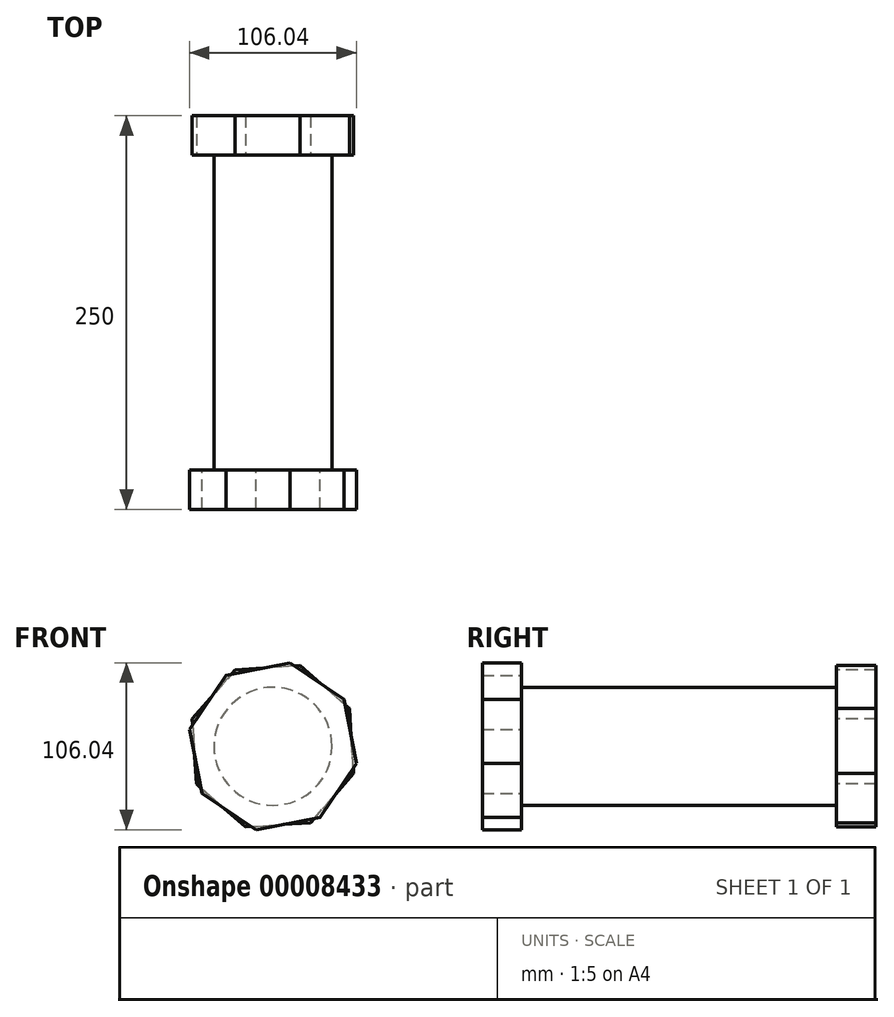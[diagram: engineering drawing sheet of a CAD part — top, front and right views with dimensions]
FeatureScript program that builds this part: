
annotation { "Feature Type Name" : "Feature", "Feature Type Description" : "" }
export const myFeature = defineFeature(function(context is Context, id is Id, definition is map)
    precondition{}
    {
        {
            var Q0;
            Q0=qCreatedBy(makeId("Front.planeOp"),FACE);
            var sketch = newSketch(context, id + "F0", { "sketchPlane" : qUnion([Q0])});
            skCircle(sketch, "E0", {"center": v(0, 0) * mm, "radius": 37.5 * mm});
            skSolve(sketch);
        }
        {
            var Q0;
            Q0 = qSketchRegion(id + "F0", true);
            extrude(context, id + "F1", {"entities" : qUnion([Q0]), "depth" : 200 * mm});
        }
        {
            var Q0;
            Q0=makeQuery(id+"F1.opExtrude","CAP_FACE",FACE,{"disambiguationData":[OSD([sQuery(id+"F0.wireOp",EDGE,"E0")])],"isStart":false});
            var sketch = newSketch(context, id + "F2", { "sketchPlane" : qUnion([Q0])});
            skCircle(sketch, "E1.cCircle", {"center": v(0, 0) * mm, "radius": 50 * mm, "construction": true});
            skLineSegment(sketch, "E1.0", {"start": v(10.83, 53.02) * mm, "end": v(45.15, 29.83) * mm});
            skLineSegment(sketch, "E1.1", {"start": v(45.15, 29.83) * mm, "end": v(53.02, -10.83) * mm});
            skLineSegment(sketch, "E1.2", {"start": v(53.02, -10.83) * mm, "end": v(29.83, -45.15) * mm});
            skLineSegment(sketch, "E1.3", {"start": v(29.83, -45.15) * mm, "end": v(-10.83, -53.02) * mm});
            skLineSegment(sketch, "E1.4", {"start": v(-10.83, -53.02) * mm, "end": v(-45.15, -29.83) * mm});
            skLineSegment(sketch, "E1.5", {"start": v(-45.15, -29.83) * mm, "end": v(-53.02, 10.83) * mm});
            skLineSegment(sketch, "E1.6", {"start": v(-53.02, 10.83) * mm, "end": v(-29.83, 45.15) * mm});
            skLineSegment(sketch, "E1.7", {"start": v(-29.83, 45.15) * mm, "end": v(10.83, 53.02) * mm});
            skPoint(sketch, "E1.0.midPoint", {"position": v(28, 41.43) * mm});
            skSolve(sketch);
        }
        {
            var Q0;
            Q0 = qSketchRegion(id + "F2", true);
            extrude(context, id + "F3", {"entities" : qUnion([Q0]), "operationType" : NewBodyOperationType.ADD, "depth" : 25 * mm});
        }
        {
            var Q0;
            Q0=makeQuery(id+"F1.opExtrude","CAP_FACE",FACE,{"disambiguationData":[OSD([sQuery(id+"F0.wireOp",EDGE,"E0")])],"isStart":true});
            var sketch = newSketch(context, id + "F4", { "sketchPlane" : qUnion([Q0])});
            skCircle(sketch, "E2.cCircle", {"center": v(0, 0) * mm, "radius": 50 * mm, "construction": true});
            skLineSegment(sketch, "E2.0", {"start": v(17.35, -51.26) * mm, "end": v(-23.98, -48.52) * mm});
            skLineSegment(sketch, "E2.1", {"start": v(-23.98, -48.52) * mm, "end": v(-51.26, -17.35) * mm});
            skLineSegment(sketch, "E2.2", {"start": v(-51.26, -17.35) * mm, "end": v(-48.52, 23.98) * mm});
            skLineSegment(sketch, "E2.3", {"start": v(-48.52, 23.98) * mm, "end": v(-17.35, 51.26) * mm});
            skLineSegment(sketch, "E2.4", {"start": v(-17.35, 51.26) * mm, "end": v(23.98, 48.52) * mm});
            skLineSegment(sketch, "E2.5", {"start": v(23.98, 48.52) * mm, "end": v(51.26, 17.35) * mm});
            skLineSegment(sketch, "E2.6", {"start": v(51.26, 17.35) * mm, "end": v(48.52, -23.98) * mm});
            skLineSegment(sketch, "E2.7", {"start": v(48.52, -23.98) * mm, "end": v(17.35, -51.26) * mm});
            skPoint(sketch, "E2.0.midPoint", {"position": v(-3.32, -49.89) * mm});
            skSolve(sketch);
        }
        {
            var Q0;
            Q0 = qSketchRegion(id + "F4", true);
            extrude(context, id + "F5", {"entities" : qUnion([Q0]), "operationType" : NewBodyOperationType.ADD, "depth" : 25 * mm});
        }
    });
